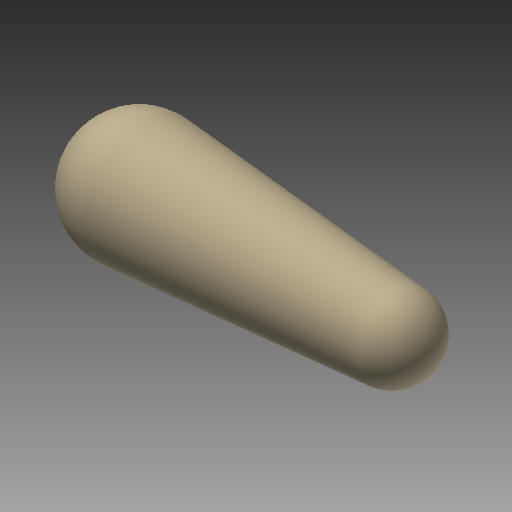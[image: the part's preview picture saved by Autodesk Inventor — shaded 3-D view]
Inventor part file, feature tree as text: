
AUTODESK INVENTOR PART (.ipt)
format: ipt  version: 2022 (Build 260153000, 153)  size: 175,616 bytes
history: native  units: mm (DEFAULTED — no unit token found)
features: other x1, revolve x1, sketch x1
ambient origin geometry x8: Origin, YZ Plane, XZ Plane, XY Plane, X Axis, Y Axis, Z Axis, Center Point
bodies: Solid1 (feature_tree)
feature tree (3):
  other  "iMan - 2D BODY"
  revolve  "Revolution1"  [1 undecoded]
  sketch  "Sketch1"  dims[d1=10.0mm d16=391.16mm d17=184.658mm d18=122.936mm d19=90.0deg]
note: 1 required parameter value undecoded (feature->parameter linkage not recoverable at this tier; creation-order binding heuristic only, values carry confidence <= 0.55)
